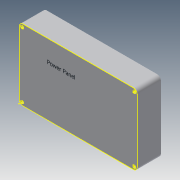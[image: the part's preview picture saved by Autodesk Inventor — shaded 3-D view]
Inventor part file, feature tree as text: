
AUTODESK INVENTOR PART (.ipt)
format: ipt  version: 2014 (Build 180170000, 170)  size: 101,888 bytes
history: native  units: in
note: dims shown in document units (in); Inventor stores cm internally (conversion verified against a paired STEP export)
features: sketch x3, extrude x1, fillet x1, hole x1
ambient origin geometry x8: Origin, YZ Plane, XZ Plane, XY Plane, X Axis, Y Axis, Z Axis, Center Point
bodies: Solid1 (feature_tree)
feature tree (6):
  extrude  "Extrusion1"  Depth=4.5in
  fillet  "Fillet1"  Radius=1.5in
  hole  "Hole1"  [1 undecoded]
  sketch  "Sketch3"  dims[d6=4.125in d7=7.125in d8=0.1875in d9=0.75in d10=0.375in d11=0.25in d12=0.5635in d13=1.0in d14=0.8108in]
  sketch  "Sketch1"  dims[d0=7.5in d1=4.5in d2=1.5in d3=0.0in]
  sketch  "Sketch2"  dims[d4=0.25in d5=7.125in]
note: 1 required parameter value undecoded (feature->parameter linkage not recoverable at this tier; creation-order binding heuristic only, values carry confidence <= 0.55)
